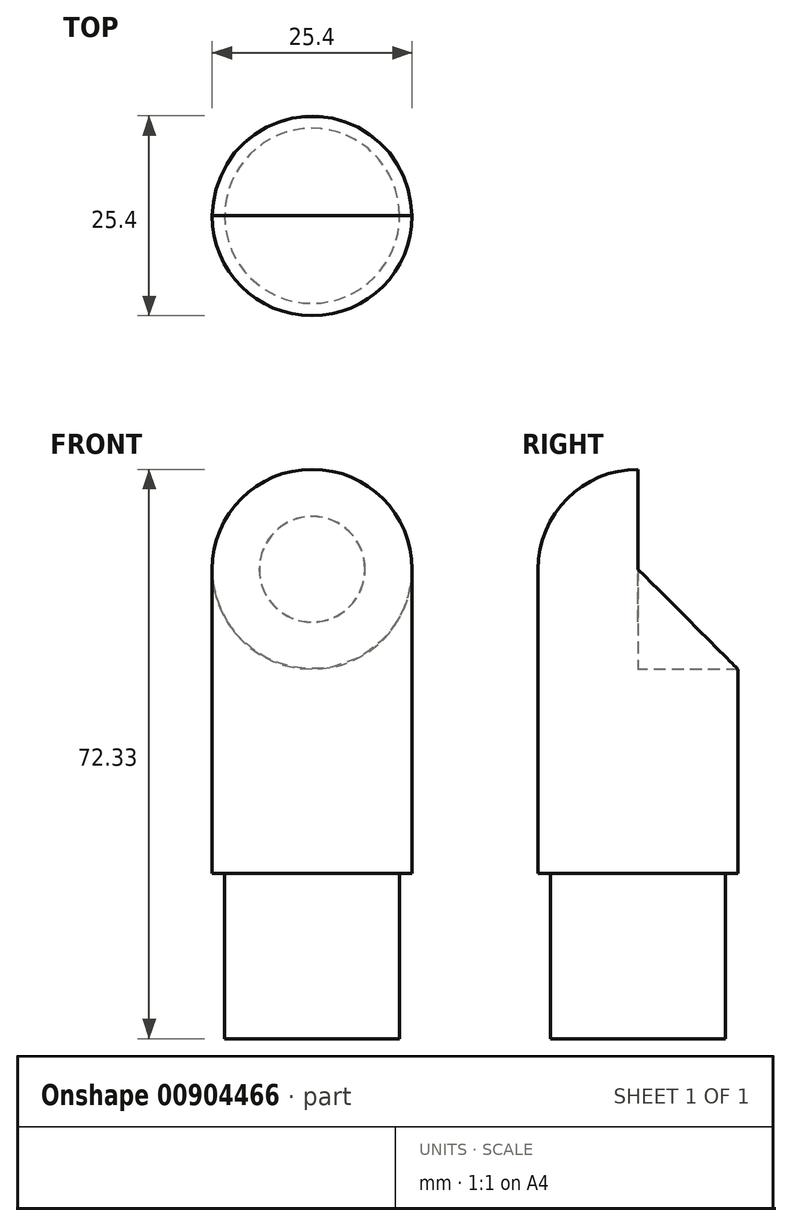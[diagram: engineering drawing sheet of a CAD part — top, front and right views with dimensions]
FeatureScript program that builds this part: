
annotation { "Feature Type Name" : "Feature", "Feature Type Description" : "" }
export const myFeature = defineFeature(function(context is Context, id is Id, definition is map)
    precondition{}
    {
        {
            var Q0;
            Q0=qCreatedBy(makeId("Front.planeOp"),FACE);
            var sketch = newSketch(context, id + "F0", { "sketchPlane" : qUnion([Q0])});
            skArc(sketch, "E0", {"start": v(0, 25.88) * mm, "mid": v(-8.98, 22.16) * mm, "end": v(-12.7, 13.18) * mm});
            skLineSegment(sketch, "E1", {"start": v(-12.7, 13.18) * mm, "end": v(-12.7, -25.45) * mm});
            skLineSegment(sketch, "E2", {"start": v(-12.7, -25.45) * mm, "end": v(-11.11, -25.45) * mm});
            skLineSegment(sketch, "E3", {"start": v(-11.11, -25.45) * mm, "end": v(-11.11, -46.45) * mm});
            skLineSegment(sketch, "E4", {"start": v(-11.11, -46.45) * mm, "end": v(0, -46.45) * mm});
            skLineSegment(sketch, "E5", {"start": v(0, 52.58) * mm, "end": v(0, -68.4) * mm, "construction": true});
            skLineSegment(sketch, "E6", {"start": v(0, 25.88) * mm, "end": v(0, -46.45) * mm});
            skSolve(sketch);
        }
        {
            var Q0;
            Q0 = qSketchRegion(id + "F0", true);
            var Q1;
            Q1=sQuery(id+"F0.wireOp",EDGE,"E5");
            revolve(context, id + "F1", {"surfaceOperationType" : NewSurfaceOperationType.NEW, "entities" : qUnion([Q0]), "axis" : qUnion([Q1]), "revolveType" : RevolveType.FULL});
        }
        {
            var Q0;
            Q0=qCreatedBy(makeId("Front.planeOp"),FACE);
            var sketch = newSketch(context, id + "F2", { "sketchPlane" : qUnion([Q0])});
            skCircle(sketch, "E7", {"center": v(0, 13.18) * mm, "radius": 12.7 * mm});
            skSolve(sketch);
        }
        {
            var Q0;
            Q0 = qSketchRegion(id + "F2", true);
            extrude(context, id + "F3", {"entities" : qUnion([Q0]), "operationType" : NewBodyOperationType.REMOVE, "endBound" : BoundingType.THROUGH_ALL, "oppositeDirection" : true, "depth" : 25 * mm, "offsetDistance" : 25 * mm});
        }
        {
            var Q0;
            Q0=qCreatedBy(makeId("Front.planeOp"),FACE);
            cPlane(context, id + "F4", {"entities" : qUnion([Q0]), "cplaneType" : CPlaneType.OFFSET, "offset" : 1 / 50.8 * mm, "width" : 150 * mm, "height" : 150 * mm});
        }
        {
            var Q0;
            Q0=qCreatedBy(id+"F4.planeOp",FACE);
            var sketch = newSketch(context, id + "F5", { "sketchPlane" : qUnion([Q0])});
            skPoint(sketch, "E8", {"position": v(0, 13.18) * mm});
            skSolve(sketch);
        }
        {
            var Q0;
            Q0=sQuery(id+"F5.wireOp",VERTEX,"E8");
            var Q1;
            Q1=makeQuery(id+"F1.opRevolve","SWEPT_BODY",BODY,{"disambiguationData":[OSD([sQuery(id+"F0.wireOp",EDGE,"E0"),sQuery(id+"F0.wireOp",EDGE,"E1"),sQuery(id+"F0.wireOp",EDGE,"E2"),sQuery(id+"F0.wireOp",EDGE,"E3"),sQuery(id+"F0.wireOp",EDGE,"E4"),sQuery(id+"F0.wireOp",EDGE,"E6")])]});
            hole(context, id + "F6", {"style" : HoleStyle.C_SINK, "endStyle" : HoleEndStyle.THROUGH, "standardTappedOrClearance" : lookupTablePath({ "fit" : "Normal", "standard" : "ISO", "size" : "M6", "type" : "Clearance" }), "standardBlindInLast" : lookupTablePath({ "fit" : "Normal", "standard" : "ISO", "size" : "M6", "type" : "Clearance" }), "holeDiameter" : 6.6 * mm, "cSinkDiameter" : 13.44 * mm, "cSinkAngle" : 90 * degree, "majorDiameter" : 5 * mm, "tappedDepth" : 7.6 * mm, "tapClearance" : 3, "startFromSketch" : true, "locations" : qUnion([Q0]), "scope" : qUnion([Q1])});
        }
    });
